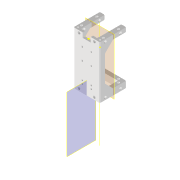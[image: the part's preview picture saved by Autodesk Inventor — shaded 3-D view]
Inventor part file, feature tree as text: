
AUTODESK INVENTOR PART (.ipt)
format: ipt  version: 2022 (Build 260153000, 153)  size: 560,128 bytes
history: native  units: mm
features: other x13, extrude x10, sketch x9, reference x6, projected_geometry x4, plane x3, hole x2, pattern_circular x2, fillet x1, mirror x1
ambient origin geometry x8: Origin, YZ Plane, XZ Plane, XY Plane, X Axis, Y Axis, Z Axis, Center Point
bodies: Solid1 (feature_tree)
feature tree (51):
  extrude  "Extrusion1"  Depth=49.8mm
  extrude  "Extrusion2"  Depth=12.0mm TaperAngle=0.0deg
  extrude  "Extrusion3"  Depth=92.0mm
  extrude  "Extrusion4"  Depth=23.45mm
  fillet  "Fillet1"  Radius=11.0mm
  plane  "Arbeitsebene1"
  plane  "Arbeitsebene2"
  hole  "Bohrung1"  [1 undecoded]
  sketch  "Skizze10"  dims[d10=70.0mm d11=23.45mm d12=11.0mm]
  hole  "Bohrung3"  [1 undecoded]
  other  "Arbeitsachse2"
  pattern_circular  "Runde Anordnung1"  [2 undecoded]
  plane  "Arbeitsebene3"
  extrude  "Extrusion7"  Depth=10.0mm
  extrude  "Extrusion8"  Depth=1.0mm
  pattern_circular  "Runde Anordnung2"  [2 undecoded]
  extrude  "Extrusion9"  Depth=1.0mm
  mirror  "Spiegeln2"
  extrude  "Extrusion10"  Depth=1.0mm
  extrude  "Extrusion12"  Depth=1.0mm
  extrude  "Extrusion13"  Depth=1.0mm
  sketch  "Sketch3"  dims[d0=49.8mm d1=49.8mm]
  sketch  "Sketch5"  dims[d2=7.8mm d3=12.0mm d4=0.0mm]
  sketch  "Skizze8"  dims[d7=92.0mm d8=0.0mm d9=2.9mm]
  reference  "Referenz1"
  reference  "Referenz2"
  reference  "Referenz3"
  sketch  "Skizze11"  dims[d13=49.8mm d14=0.0mm d28=2.8mm]
  projected_geometry  "Projizierte Kontur2"
  reference  "Referenz39"
  reference  "Referenz40"
  reference  "Referenz41"
  sketch  "Skizze16"  dims[d29=2.8mm d30=20.0mm d31=0.0mm]
  projected_geometry  "Projizierte Kontur3"
  sketch  "Skizze17"  dims[d40=2.0mm]
  projected_geometry  "Projizierte Kontur4"
  sketch  "Sketch19"  dims[d43=4.8mm d44=6.0mm d45=4.0mm d46=2.0mm d47=90.0deg d48=12.0mm d49=20.594885mm]
  sketch  "Skizze20"  dims[d57=0.0mm d58=10.0mm d59=10.0mm d69=4.8mm d70=6.0mm d71=4.0mm d72=2.0mm d73=90.0deg d74=12.0mm d75=20.594885mm d90=2.8mm d91=2.8mm d92=40.0mm d93=4.9mm d94=4.9mm d95=4.9mm d96=40.0mm d97=360.0deg d99=10.0mm d100=0.0mm d101=10.0mm d102=0.0mm d103=30.0mm d104=180.0deg d109=135.0deg d110=135.0deg d111=10.0mm d112=0.0mm d113=2.8mm d114=2.8mm d115=10.0mm d116=0.0mm d121=23.432281mm d122=45.0deg d123=2.9mm d125=21.0mm d128=7.05mm d129=20.0mm d131=17.0mm d132=20.0mm d134=55.0mm d151=15.0mm d152=18.0mm d153=10.0mm d154=0.0mm d155=40.0mm d156=94.0mm d157=2.9mm d159=20.0mm d161=38.0mm d162=10.0mm d164=10.0mm d166=15.0mm d167=2.9mm d168=2.9mm d169=15.0mm d170=15.0mm d171=20.0mm d173=38.0mm d174=10.0mm d176=10.0mm d178=4.35mm d179=4.35mm d180=10.24mm d181=10.56mm d182=3.5mm d183=3.5mm d184=4.0mm d185=4.0mm d186=4.0mm d187=4.0mm d188=0.0mm d189=0.0mm d60=0.872665mm d76=1.0mm d77=1.0mm d78=1.0mm d79=0.15mm d80=0.25mm d81=0.375mm d82=14.3117mm d83=0.75mm d84=20.594885mm d85=0.0625mm d86=0.75mm d87=0.375mm d105=14.3117mm d106=0.75mm d107=20.594885mm d108=0.0625mm]
  projected_geometry  "Projizierte Kontur6"
  other  "Assembly_Cube_Z-Stage_NEMA11_china_Borstel.iam"
  other  "10_Base_puzzle_IM:1"
  other  "Assembly_Cube_Z-Stage_NEMA11_china_multidirection.iam"
  other  "00_Linear_Stage_NEMA11_china:1"
  other  "Actuator_movable"
  other  "30_Linear_Stage_NEMA11_China_lid:1"
  other  "Assembly_Cube_Z-Stage_NEMA11_china_universal_25mm.iam"
  other  "10_Base_puzzle_v3:6"
  other  "10_Base_puzzle_v3:5"
  other  "30_Linear_Stage_NEMA11_China_lid_universal_extender_v2:1"
  other  "00_Linear_Stage_NEMA11_25mm_china:1"
  other  "Nema11:1"
note: 6 required parameter values undecoded (feature->parameter linkage not recoverable at this tier; creation-order binding heuristic only, values carry confidence <= 0.55)
